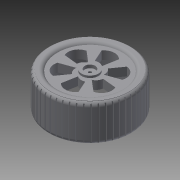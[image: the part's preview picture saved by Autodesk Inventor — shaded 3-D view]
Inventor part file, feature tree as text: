
AUTODESK INVENTOR PART (.ipt)
format: ipt  version: 2015 (Build 190159000, 159)  size: 542,208 bytes
history: native  units: mm
features: sketch x8, extrude x5, fillet x3, hole x2, pattern_circular x2, revolve x1, projected_geometry x1
ambient origin geometry x8: Origin, YZ Plane, XZ Plane, XY Plane, X Axis, Y Axis, Z Axis, Center Point
bodies: Solid1 (feature_tree)
feature tree (22):
  revolve  "Revolution1"  [1 undecoded]
  fillet  "Fillet1"  Radius=35.0mm
  extrude  "Extrusion1"  Depth=4.0mm
  fillet  "Fillet2"  Radius=75.0mm
  hole  "Hole1"  [1 undecoded]
  extrude  "Extrusion2"  Depth=10.0mm TaperAngle=0.0deg
  extrude  "Extrusion3"  Depth=4.0mm
  fillet  "Fillet3"  Radius=60.0mm
  pattern_circular  "Circular Pattern1"  [2 undecoded]
  hole  "Hole2"  [1 undecoded]
  extrude  "Extrusion4"  Depth=10.0mm
  pattern_circular  "Circular Pattern2"  [2 undecoded]
  extrude  "Extrusion5"  [1 undecoded]
  sketch  "Sketch1"  dims[d2=5.0mm d3=35.0mm d4=35.0mm]
  sketch  "Sketch2"  dims[d5=90.0deg d6=4.0mm d7=75.0mm]
  sketch  "Sketch3"  dims[d8=10.0mm d9=0.0mm d10=4.0mm]
  sketch  "Sketch4"  dims[d11=3.0mm d12=6.0mm d13=10.0mm d14=3.0mm d15=90.0deg d16=8.0mm d17=20.594885mm d18=10.0mm d19=0.0mm]
  sketch  "Sketch5"  dims[d20=2.0mm d21=0.0mm d22=4.0mm d23=60.0mm d24=360.0deg]
  sketch  "Sketch6"  dims[d26=10.0mm d27=6.0mm d28=10.0mm d29=3.0mm d30=90.0deg d31=2.0mm d32=0.0mm]
  sketch  "Sketch7"  dims[d33=1.0mm]
  sketch  "Sketch8"  dims[d34=1.0mm d35=10.0mm d36=0.0mm d37=500.0mm d38=360.0deg d40=16.0mm d41=2.0mm d42=0.0mm]
  projected_geometry  "Projected Loop1"
note: 8 required parameter values undecoded (feature->parameter linkage not recoverable at this tier; creation-order binding heuristic only, values carry confidence <= 0.55)